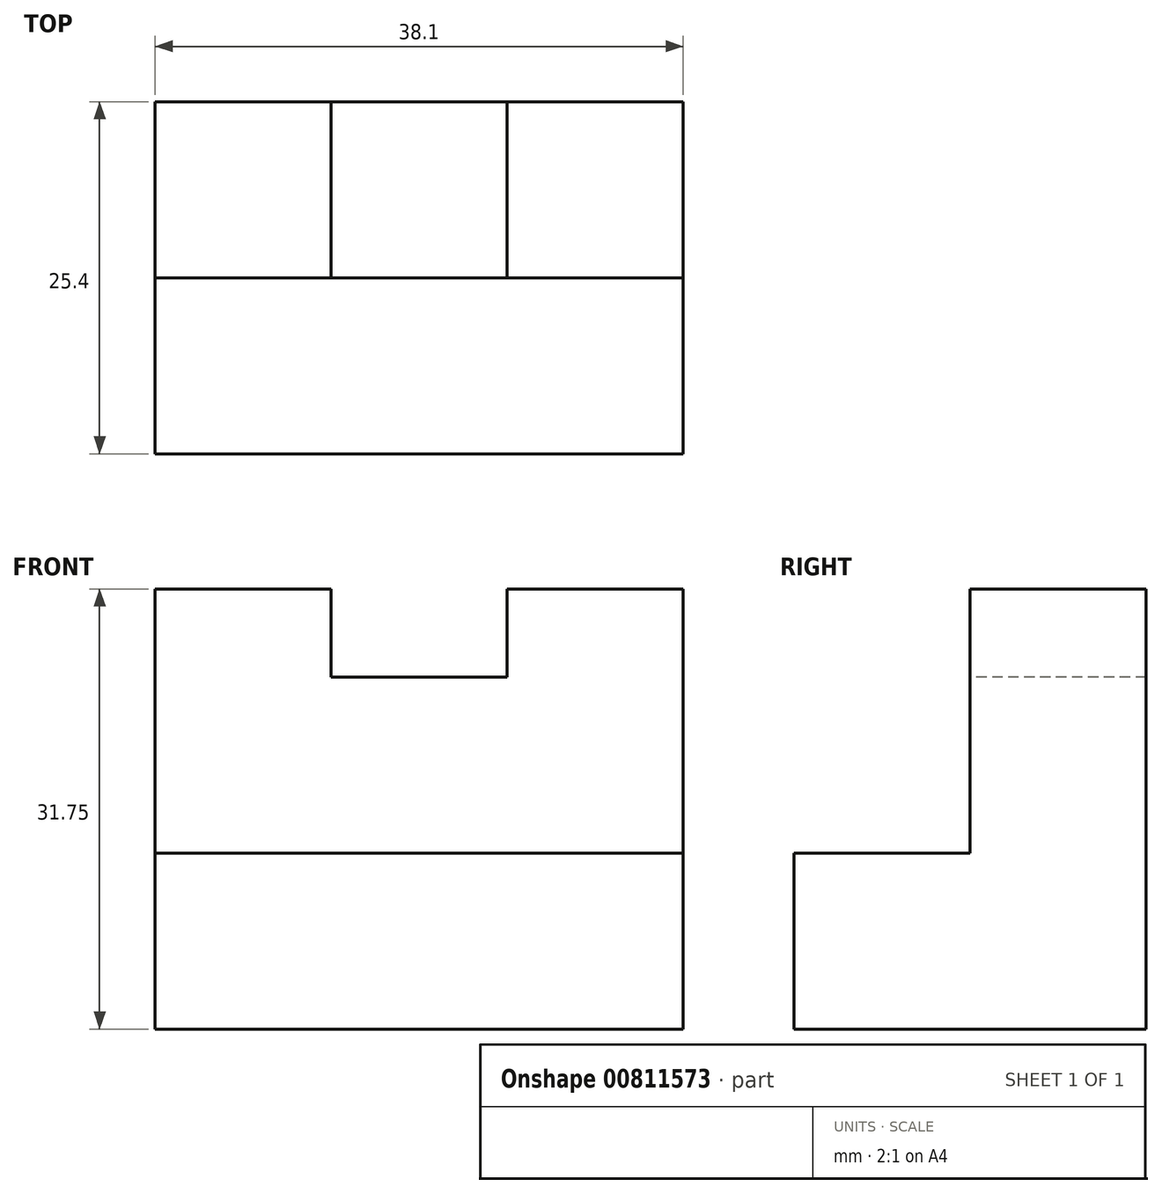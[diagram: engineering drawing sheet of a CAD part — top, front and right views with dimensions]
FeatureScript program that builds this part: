
annotation { "Feature Type Name" : "Feature", "Feature Type Description" : "" }
export const myFeature = defineFeature(function(context is Context, id is Id, definition is map)
    precondition{}
    {
        {
            var Q0;
            Q0=qCreatedBy(makeId("Right.planeOp"),FACE);
            var sketch = newSketch(context, id + "F0", { "sketchPlane" : qUnion([Q0])});
            skLineSegment(sketch, "E0", {"start": v(0, 0) * mm, "end": v(25.4, 0) * mm});
            skLineSegment(sketch, "E1", {"start": v(25.4, 0) * mm, "end": v(25.4, 31.75) * mm});
            skLineSegment(sketch, "E2", {"start": v(25.4, 31.75) * mm, "end": v(12.7, 31.75) * mm});
            skLineSegment(sketch, "E3", {"start": v(12.7, 31.75) * mm, "end": v(12.7, 12.7) * mm});
            skLineSegment(sketch, "E4", {"start": v(12.7, 12.7) * mm, "end": v(0, 12.7) * mm});
            skLineSegment(sketch, "E5", {"start": v(0, 12.7) * mm, "end": v(0, 0) * mm});
            skSolve(sketch);
        }
        {
            var Q0;
            Q0 = qSketchRegion(id + "F0", true);
            extrude(context, id + "F1", {"entities" : qUnion([Q0]), "depth" : 38.1 * mm, "offsetDistance" : 25.4 * mm});
        }
        {
            var Q0;
            Q0=makeQuery(id+"F1.opExtrude","SWEPT_FACE",FACE,{"disambiguationData":[OSD([sQuery(id+"F0.wireOp",EDGE,"E2")])]});
            var sketch = newSketch(context, id + "F2", { "sketchPlane" : qUnion([Q0])});
            skLineSegment(sketch, "E6", {"start": v(0, 25.4) * mm, "end": v(12.7, 25.4) * mm});
            skLineSegment(sketch, "E7", {"start": v(38.1, 25.4) * mm, "end": v(25.4, 25.4) * mm});
            skLineSegment(sketch, "E8", {"start": v(12.7, 25.4) * mm, "end": v(12.7, 12.7) * mm});
            skLineSegment(sketch, "E9", {"start": v(25.4, 25.4) * mm, "end": v(25.4, 12.7) * mm});
            skLineSegment(sketch, "E10", {"start": v(38.1, 25.4) * mm, "end": v(38.1, 12.7) * mm});
            skLineSegment(sketch, "E11", {"start": v(38.1, 12.7) * mm, "end": v(25.4, 12.7) * mm});
            skLineSegment(sketch, "E12", {"start": v(0, 25.4) * mm, "end": v(0, 12.7) * mm});
            skLineSegment(sketch, "E13", {"start": v(0, 12.7) * mm, "end": v(12.7, 12.7) * mm});
            skSolve(sketch);
        }
        {
            var Q0;
            {var subQ0=sQuery(id+"F2.wireOp",EDGE,"E8");Q0=makeQuery(id+"F2.imprint","IMPRINT",FACE,{"disambiguationData":[TD([[makeQuery(id+"F2.imprint","IMPRINT",EDGE,{"derivedFrom":subQ0}),1.0]])]});}
            extrude(context, id + "F3", {"entities" : qUnion([Q0]), "operationType" : NewBodyOperationType.REMOVE, "oppositeDirection" : true, "depth" : 6.35 * mm, "offsetDistance" : 25.4 * mm});
        }
    });
